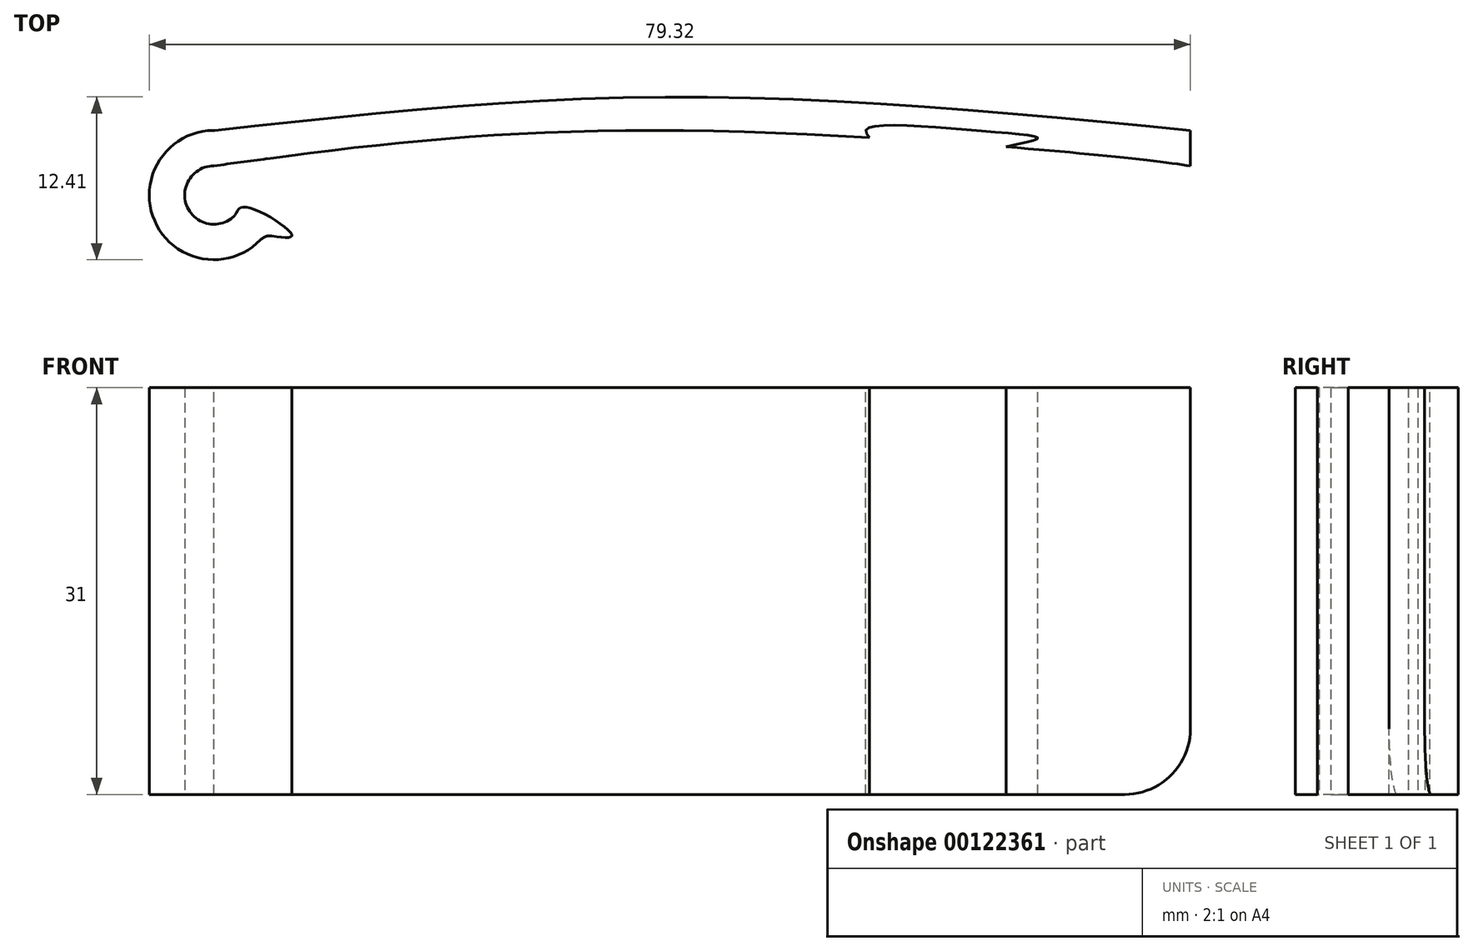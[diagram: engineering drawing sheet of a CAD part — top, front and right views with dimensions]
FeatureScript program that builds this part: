
annotation { "Feature Type Name" : "Feature", "Feature Type Description" : "" }
export const myFeature = defineFeature(function(context is Context, id is Id, definition is map)
    precondition{}
    {
        {
            var Q0;
            Q0=qCreatedBy(makeId("Top.planeOp"),FACE);
            var sketch = newSketch(context, id + "F0", { "sketchPlane" : qUnion([Q0])});
            skArc(sketch, "E0", {"start": v(0.32, 2.2) * mm, "mid": v(-2.1, -0.74) * mm, "end": v(1.63, -1.51) * mm});
            skLineSegment(sketch, "E1", {"start": v(0, 0) * mm, "end": v(48.47, 0) * mm, "construction": true});
            skLineSegment(sketch, "E2", {"start": v(0, 2.23) * mm, "end": v(0, 4.93) * mm, "construction": true});
            skLineSegment(sketch, "E3", {"start": v(-4.93, 0) * mm, "end": v(-4.93, 4.93) * mm, "construction": true});
            skLineSegment(sketch, "E4", {"start": v(-4.93, 4.93) * mm, "end": v(74.4, 4.93) * mm, "construction": true});
            skLineSegment(sketch, "E5", {"start": v(34.73, 4.93) * mm, "end": v(34.73, 7.48) * mm, "construction": true});
            skFitSpline(sketch, "E6", {"points": [v(0, 4.93) * mm, v(34.73, 7.48) * mm, v(74.4, 4.93) * mm], "startDerivative": vector(70.64, 7.74) * mm, "endDerivative": vector(78.06, -7.57) * mm});
            skArc(sketch, "E7", {"start": v(49.68, 1.19) * mm, "mid": v(48.48, -0.15) * mm, "end": v(50, -1.12) * mm});
            skFitSpline(sketch, "E8", {"points": [v(0, 2.23) * mm, v(34.73, 4.93) * mm, v(74.37, 2.23) * mm, v(75.64, 2.23) * mm, v(74.4, 4.93) * mm], "startDerivative": vector(78.51, 10.74) * mm, "endDerivative": vector(-17.4, 30.58) * mm});
            skFitSpline(sketch, "E9", {"points": [v(50, -1.12) * mm, v(52.94, 0) * mm, v(55.89, 2.38) * mm, v(62.74, 4.3) * mm, v(57.96, 4.93) * mm, v(49.68, 4.93) * mm, v(50.71, 3.34) * mm, v(49.68, 1.19) * mm], "startDerivative": vector(26.33, 6.62) * mm, "endDerivative": vector(-17.77, -20.2) * mm});
            skArc(sketch, "E10.trimOffspring", {"start": v(0, 4.93) * mm, "mid": v(-4.43, -2.16) * mm, "end": v(3.89, -3.03) * mm});
            skFitSpline(sketch, "E11", {"points": [v(0, 2.23) * mm, v(2.78, 2.23) * mm, v(4.07, 2.78) * mm], "startDerivative": vector(5.24, -0.39) * mm, "endDerivative": vector(2.77, 1.6) * mm});
            skFitSpline(sketch, "E12", {"points": [v(1.63, -1.51) * mm, v(2.37, -0.9) * mm, v(5.94, -3.03) * mm, v(3.89, -3.03) * mm], "startDerivative": vector(1.82, 4.33) * mm, "endDerivative": vector(-9.95, 1.63) * mm});
            skSolve(sketch);
        }
        {
            var Q0;
            Q0=makeQuery(id+"F0.imprint","IMPRINT",FACE,{"disambiguationData":[TD([[makeQuery(id+"F0.imprint","IMPRINT",EDGE,{"derivedFrom":sQuery(id+"F0.wireOp",EDGE,"E6")}),-1.0]])]});
            extrude(context, id + "F1", {"entities" : qUnion([Q0]), "depth" : 31 * mm});
        }
        {
            var Q0;
            Q0=makeQuery(id+"F1.opExtrude","SWEPT_EDGE",EDGE,{"disambiguationData":[OSD([sQuery(id+"F0.wireOp",EDGE,"E0"),sQuery(id+"F0.wireOp",EDGE,"vMBzHM69-rA8N-9GM1-xJLN-n5vkRMWM7Yqb")])]});
            var Q1;
            Q1=makeQuery(id+"F1.opExtrude","SWEPT_EDGE",EDGE,{"disambiguationData":[OSD([sQuery(id+"F0.wireOp",EDGE,"vMBzHM69-rA8N-9GM1-xJLN-n5vkRMWM7Yqb"),sQuery(id+"F0.wireOp",EDGE,"E10.trimOffspring")])]});
            var Q2;
            Q2=makeQuery(id+"F1.opExtrude","SWEPT_EDGE",EDGE,{"disambiguationData":[OSD([sQuery(id+"F0.wireOp",EDGE,"E8"),sQuery(id+"F0.wireOp",EDGE,"E11")])]});
            fillet(context, id + "F2", {"entities" : qUnion([Q0, Q1, Q2]), "radius" : 1 * mm, "tangentPropagation" : true, "allowEdgeOverflow" : false});
        }
        {
            var Q0;
            Q0=makeQuery(id+"F1.opExtrude","CAP_FACE",FACE,{"disambiguationData":[OSD([sQuery(id+"F0.wireOp",EDGE,"E0"),sQuery(id+"F0.wireOp",EDGE,"E6"),sQuery(id+"F0.wireOp",EDGE,"E7"),sQuery(id+"F0.wireOp",EDGE,"E8"),sQuery(id+"F0.wireOp",EDGE,"E9"),sQuery(id+"F0.wireOp",EDGE,"E9"),sQuery(id+"F0.wireOp",EDGE,"E8"),sQuery(id+"F0.wireOp",EDGE,"E10.trimOffspring"),sQuery(id+"F0.wireOp",EDGE,"E11"),sQuery(id+"F0.wireOp",EDGE,"E12")])],"isStart":false});
            var sketch = newSketch(context, id + "F3", { "sketchPlane" : qUnion([Q0])});
            skLineSegment(sketch, "E13", {"start": v(74.4, 4.93) * mm, "end": v(74.4, 2.22) * mm});
            skSolve(sketch);
        }
        {
            var Q0;
            {var subQ0=sQuery(id+"F3.wireOp",EDGE,"E13");Q0=makeQuery(id+"F3.imprint","IMPRINT",FACE,{"disambiguationData":[TD([[makeQuery(id+"F3.imprint","IMPRINT",EDGE,{"derivedFrom":subQ0}),1.0]])]});}
            extrude(context, id + "F4", {"entities" : qUnion([Q0]), "operationType" : NewBodyOperationType.REMOVE, "endBound" : BoundingType.THROUGH_ALL, "oppositeDirection" : true, "depth" : 25 * mm});
        }
        {
            var Q0;
            Q0=makeQuery(id+"F4.boolean.opBoolean","INTERSECT",EDGE,{"derivedFrom":[makeQuery(id+"F1.opExtrude","CAP_FACE",FACE,{"disambiguationData":[OSD([sQuery(id+"F0.wireOp",EDGE,"E0"),sQuery(id+"F0.wireOp",EDGE,"E6"),sQuery(id+"F0.wireOp",EDGE,"E7"),sQuery(id+"F0.wireOp",EDGE,"E8"),sQuery(id+"F0.wireOp",EDGE,"E9"),sQuery(id+"F0.wireOp",EDGE,"E9"),sQuery(id+"F0.wireOp",EDGE,"E8"),sQuery(id+"F0.wireOp",EDGE,"E10.trimOffspring"),sQuery(id+"F0.wireOp",EDGE,"E11"),sQuery(id+"F0.wireOp",EDGE,"E12")])],"isStart":true}),makeQuery(id+"F4.opExtrude","SWEPT_FACE",FACE,{"disambiguationData":[OSD([sQuery(id+"F3.wireOp",EDGE,"E13")])]})]});
            var Q1;
            Q1=makeQuery(id+"F4.boolean.opBoolean","COPY",EDGE,{"derivedFrom":makeQuery(id+"F4.opExtrude","CAP_EDGE",EDGE,{"disambiguationData":[OSD([sQuery(id+"F3.wireOp",EDGE,"E13")])],"isStart":true})});
            fillet(context, id + "F5", {"entities" : qUnion([Q0, Q1]), "radius" : 5 * mm, "tangentPropagation" : true, "allowEdgeOverflow" : false});
        }
    });
